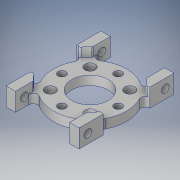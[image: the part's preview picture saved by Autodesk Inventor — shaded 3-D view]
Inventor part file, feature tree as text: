
AUTODESK INVENTOR PART (.ipt)
format: ipt  version: 2019 (Build 230136000, 136)  size: 187,904 bytes
history: native  units: in
note: dims shown in document units (in); Inventor stores cm internally (conversion verified against a paired STEP export)
features: mirror x1
ambient origin geometry x8: Origin, YZ Plane, XZ Plane, XY Plane, X Axis, Y Axis, Z Axis, Center Point
bodies: Solid1 (feature_tree)
feature tree (1):
  mirror  "Mirror6"
